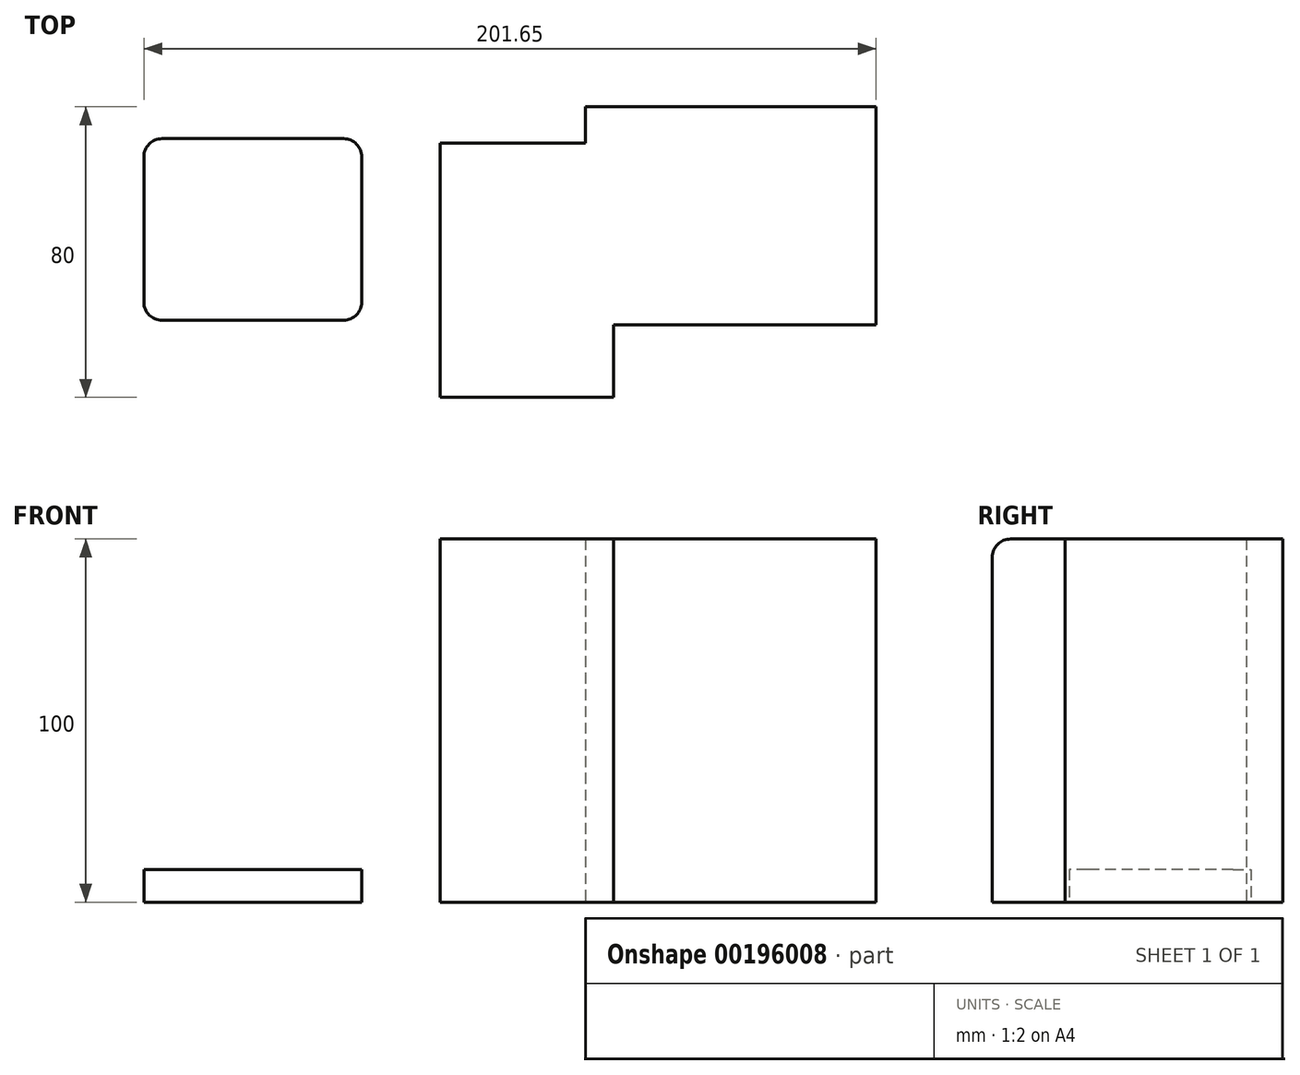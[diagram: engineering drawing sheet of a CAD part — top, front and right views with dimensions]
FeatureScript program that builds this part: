
annotation { "Feature Type Name" : "Feature", "Feature Type Description" : "" }
export const myFeature = defineFeature(function(context is Context, id is Id, definition is map)
    precondition{}
    {
        {
            var Q0;
            Q0=qCreatedBy(makeId("Top.planeOp"),FACE);
            var sketch = newSketch(context, id + "F0", { "sketchPlane" : qUnion([Q0])});
            skLineSegment(sketch, "E0.bottom", {"start": v(-19.7, 29.7) * mm, "end": v(60.3, 29.7) * mm});
            skLineSegment(sketch, "E0.top", {"start": v(-12.05, -30.3) * mm, "end": v(60.3, -30.3) * mm});
            skLineSegment(sketch, "E0.left", {"start": v(-19.7, 29.7) * mm, "end": v(-19.7, 19.7) * mm});
            skLineSegment(sketch, "E0.right", {"start": v(60.3, 29.7) * mm, "end": v(60.3, -30.3) * mm});
            skLineSegment(sketch, "E1.bottom", {"start": v(-59.7, 19.7) * mm, "end": v(-19.7, 19.7) * mm});
            skLineSegment(sketch, "E1.top", {"start": v(-59.7, -50.3) * mm, "end": v(-12.05, -50.3) * mm});
            skLineSegment(sketch, "E1.left", {"start": v(-59.7, 19.7) * mm, "end": v(-59.7, -50.3) * mm});
            skLineSegment(sketch, "E1.right", {"start": v(-12.05, -30.3) * mm, "end": v(-12.05, -50.3) * mm});
            skSolve(sketch);
        }
        {
            var Q0;
            Q0 = qSketchRegion(id + "F0", true);
            extrude(context, id + "F1", {"entities" : qUnion([Q0]), "depth" : 100 * mm});
        }
        {
            var Q0;
            Q0=makeQuery(id+"F1.opExtrude","CAP_EDGE",EDGE,{"disambiguationData":[OSD([sQuery(id+"F0.wireOp",EDGE,"E1.top")])],"isStart":false});
            fillet(context, id + "F2", {"entities" : qUnion([Q0]), "radius" : 5 * mm, "tangentPropagation" : true, "allowEdgeOverflow" : false});
        }
        {
            var Q0;
            Q0=qCreatedBy(makeId("Top.planeOp"),FACE);
            var sketch = newSketch(context, id + "F3", { "sketchPlane" : qUnion([Q0])});
            skLineSegment(sketch, "E2.bottom", {"start": v(-141.35, 20.94) * mm, "end": v(-81.35, 20.94) * mm});
            skLineSegment(sketch, "E2.top", {"start": v(-141.35, -29.06) * mm, "end": v(-81.35, -29.06) * mm});
            skLineSegment(sketch, "E2.left", {"start": v(-141.35, 20.94) * mm, "end": v(-141.35, -29.06) * mm});
            skLineSegment(sketch, "E2.right", {"start": v(-81.35, 20.94) * mm, "end": v(-81.35, -29.06) * mm});
            skSolve(sketch);
        }
        {
            var Q0;
            Q0 = qSketchRegion(id + "F3", true);
            extrude(context, id + "F4", {"entities" : qUnion([Q0]), "depth" : 9 * mm});
        }
        {
            var Q0;
            Q0=makeQuery(id+"F4.opExtrude","SWEPT_EDGE",EDGE,{"disambiguationData":[OSD([sQuery(id+"F3.wireOp",EDGE,"E2.bottom"),sQuery(id+"F3.wireOp",EDGE,"E2.left")])]});
            var Q1;
            Q1=makeQuery(id+"F4.opExtrude","SWEPT_EDGE",EDGE,{"disambiguationData":[OSD([sQuery(id+"F3.wireOp",EDGE,"E2.top"),sQuery(id+"F3.wireOp",EDGE,"E2.left")])]});
            var Q2;
            Q2=makeQuery(id+"F4.opExtrude","SWEPT_EDGE",EDGE,{"disambiguationData":[OSD([sQuery(id+"F3.wireOp",EDGE,"E2.top"),sQuery(id+"F3.wireOp",EDGE,"E2.right")])]});
            var Q3;
            Q3=makeQuery(id+"F4.opExtrude","SWEPT_EDGE",EDGE,{"disambiguationData":[OSD([sQuery(id+"F3.wireOp",EDGE,"E2.bottom"),sQuery(id+"F3.wireOp",EDGE,"E2.right")])]});
            fillet(context, id + "F5", {"entities" : qUnion([Q0, Q1, Q2, Q3]), "radius" : 5 * mm, "tangentPropagation" : true, "allowEdgeOverflow" : false});
        }
    });
